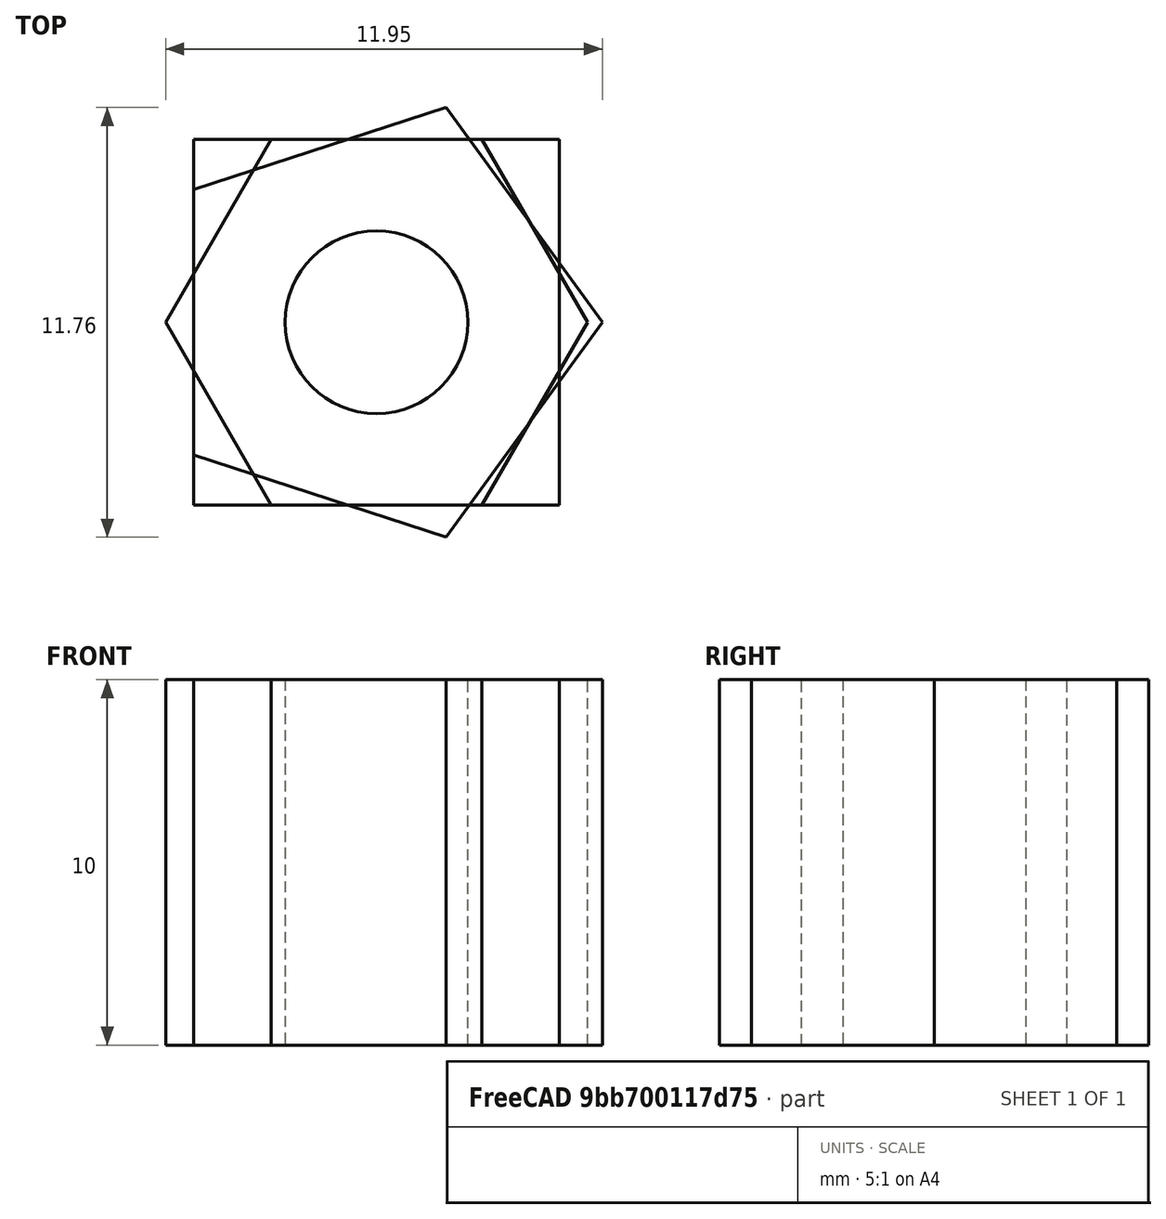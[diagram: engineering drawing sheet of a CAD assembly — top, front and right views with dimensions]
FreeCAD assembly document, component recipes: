
FREECAD ASSEMBLY — COMPONENT RECIPES ("xchg-components")

This assembly document has 6 components, labeled P0..P5 below (a component is one placed body or linked part). 6 of them carry a construction recipe — the FreeCAD feature program that regenerates the part from scratch, quoted from this document or its linked companion documents; the rest are supplied as boundary geometry only. No exploded tour is included for this assembly.
COMPONENT P0 — recipe-attached ("Cube 001", modeled in this document).
Construction recipe (the document's own serialized feature program — sketch geometry with constraints, then the solid features built on it; lengths are millimeters unless a unit is written):

FEATURE [Sketcher::SketchObject] Sketch001
  MapMode = 5
  Support = -> [XY_Plane001]
  sketch-geometry (5):
    g0: LineSegment StartX=5 StartY=5 StartZ=0 EndX=-5 EndY=5 EndZ=0
    g1: LineSegment StartX=-5 StartY=5 StartZ=0 EndX=-5 EndY=-5 EndZ=0
    g2: LineSegment StartX=-5 StartY=-5 StartZ=0 EndX=5 EndY=-5 EndZ=0
    g3: LineSegment StartX=5 StartY=-5 StartZ=0 EndX=5 EndY=5 EndZ=0
    g4: Circle [constr] CenterX=0 CenterY=0 CenterZ=0 NormalX=0 NormalY=0 NormalZ=1 AngleXU=0 Radius=7.07107
  constraints (14):
    c: Coincident(g0,g1)
    c: Coincident(g1,g2)
    c: Coincident(g2,g3)
    c: Coincident(g3,g0)
    c: Equal(g0,g1)
    c: Equal(g0,g2)
    c: Equal(g0,g3)
    c: PointOnObject(g0,g4)
    c: PointOnObject(g1,g4)
    c: PointOnObject(g2,g4)
    c: PointOnObject(g3,g4)
    c: Coincident(g4,g-1)
    c: Horizontal(g0)
    c: Distance(g2) = 10
FEATURE [PartDesign::Pad] Pad001
  ClaimChildren = false
  Length = 10
  Length2 = 100
  Profile = -> Sketch001
  Type = 0
FEATURE [PartDesign::Body] Body001  label="Cube 000"
  Group = -> [Sketch001,Pad001]
  Origin = -> Origin001
  Tip = -> Pad001
COMPONENT P1 — recipe-attached ("Cylinder 001", modeled in this document).
Construction recipe (the document's own serialized feature program — sketch geometry with constraints, then the solid features built on it; lengths are millimeters unless a unit is written):

FEATURE [Sketcher::SketchObject] Sketch
  MapMode = 5
  Support = -> [XY_Plane]
  sketch-geometry (1):
    g0: Circle CenterX=0 CenterY=0 CenterZ=0 NormalX=0 NormalY=0 NormalZ=1 AngleXU=0 Radius=2.5
  constraints (2):
    c: Coincident(g0,g-1)
    c: Diameter(g0) = 5
FEATURE [PartDesign::Pad] Pad
  ClaimChildren = false
  Length = 10
  Length2 = 100
  Profile = -> Sketch
  Type = 0
FEATURE [PartDesign::Body] Body  label="Cylinder 000"
  Group = -> [Sketch,Pad]
  Origin = -> Origin
  Tip = -> Pad
COMPONENT P2 — same part as P1; its construction recipe is shown at P1.
COMPONENT P3 — recipe-attached ("Pentagon 001", modeled in this document).
Construction recipe (the document's own serialized feature program — sketch geometry with constraints, then the solid features built on it; lengths are millimeters unless a unit is written):

FEATURE [Sketcher::SketchObject] Sketch002
  MapMode = 5
  Support = -> [XY_Plane002]
  sketch-geometry (6):
    g0: LineSegment StartX=6.18034 StartY=0 StartZ=0 EndX=1.90983 EndY=5.87785 EndZ=0
    g1: LineSegment StartX=1.90983 StartY=5.87785 StartZ=0 EndX=-5 EndY=3.63271 EndZ=0
    g2: LineSegment StartX=-5 StartY=3.63271 StartZ=0 EndX=-5 EndY=-3.63271 EndZ=0
    g3: LineSegment StartX=-5 StartY=-3.63271 StartZ=0 EndX=1.90983 EndY=-5.87785 EndZ=0
    g4: LineSegment StartX=1.90983 StartY=-5.87785 StartZ=0 EndX=6.18034 EndY=0 EndZ=0
    g5: Circle [constr] CenterX=0 CenterY=0 CenterZ=0 NormalX=0 NormalY=0 NormalZ=1 AngleXU=0 Radius=6.18034
  constraints (14):
    c: Coincident(g0,g1)
    c: Coincident(g1,g2)
    c: Coincident(g2,g3)
    c: Coincident(g3,g4)
    c: Coincident(g4,g0)
    c: Equal(g0, g1-g4) x4
    c: PointOnObject(g0,g5)
    c: PointOnObject(g1,g5)
    c: PointOnObject(g2,g5)
    c: PointOnObject(g3,g5)
    c: PointOnObject(g4,g5)
    c: Coincident(g5,g-1)
    c: PointOnObject(g4,g-1)
    c: DistanceX(g2,g-1) = 5
FEATURE [PartDesign::Pad] Pad002
  ClaimChildren = false
  Length = 10
  Length2 = 100
  Profile = -> Sketch002
  Type = 0
FEATURE [PartDesign::Body] Body002  label="Pentagon 000"
  Group = -> [Sketch002,Pad002]
  Origin = -> Origin002
  Tip = -> Pad002
COMPONENT P4 — same part as P1; its construction recipe is shown at P1.
COMPONENT P5 — recipe-attached ("Hexagon001", modeled in this document).
Construction recipe (the document's own serialized feature program — sketch geometry with constraints, then the solid features built on it; lengths are millimeters unless a unit is written):

FEATURE [Sketcher::SketchObject] Sketch003
  MapMode = 5
  Support = -> [XY_Plane003]
  sketch-geometry (7):
    g0: LineSegment StartX=5.7735 StartY=0 StartZ=0 EndX=2.88675 EndY=5 EndZ=0
    g1: LineSegment StartX=2.88675 StartY=5 StartZ=0 EndX=-2.88675 EndY=5 EndZ=0
    g2: LineSegment StartX=-2.88675 StartY=5 StartZ=0 EndX=-5.7735 EndY=2.0126e-12 EndZ=0
    g3: LineSegment StartX=-5.7735 StartY=2.0126e-12 StartZ=0 EndX=-2.88675 EndY=-5 EndZ=0
    g4: LineSegment StartX=-2.88675 StartY=-5 StartZ=0 EndX=2.88675 EndY=-5 EndZ=0
    g5: LineSegment StartX=2.88675 StartY=-5 StartZ=0 EndX=5.7735 EndY=0 EndZ=0
    g6: Circle [constr] CenterX=0 CenterY=0 CenterZ=0 NormalX=0 NormalY=0 NormalZ=1 AngleXU=0 Radius=5.7735
  constraints (16):
    c: Coincident(g0,g1)
    c: Coincident(g1,g2)
    c: Coincident(g2,g3)
    c: Coincident(g3,g4)
    c: Coincident(g4,g5)
    c: Coincident(g5,g0)
    c: Equal(g0, g1-g5) x5
    c: PointOnObject(g0,g6)
    c: PointOnObject(g1,g6)
    c: PointOnObject(g2,g6)
    c: PointOnObject(g3,g6)
    c: PointOnObject(g4,g6)
    c: PointOnObject(g5,g6)
    c: Coincident(g6,g-1)
    c: PointOnObject(g5,g-1)
    c: Distance(g0,g4) = 10
FEATURE [PartDesign::Pad] Pad003
  ClaimChildren = false
  Length = 10
  Length2 = 100
  Profile = -> Sketch003
  Type = 0
FEATURE [PartDesign::Body] Body003  label="Hexagon"
  Group = -> [Sketch003,Pad003]
  Origin = -> Origin003
  Tip = -> Pad003
PROVENANCE & LICENSES
A FreeCAD (.FCStd) document from a public repository crawl; recipes are the document's own serialized feature recipes (and, for linked parts, companion documents' recipes).
License: as declared in the source repository (recorded in the dataset sidecar).
